# Revit family: 306_R4_D_
name_source: partatom
category: Pipe Accessories
units: mm (PartAtom-declared; Revit-internal decimal feet)

## family parameters
Always vertical = Yes
Cut with Voids When Loaded = No
Part Type = Valve - Breaks Into
Round Connector Dimension = Use Diameter
Shared = No
Work Plane-Based = No

## types (12) — shared parameters
CAT0 = Yes
Description = Characterised control valve, 2-way, External thread
L2D_Min = 3048 mm  [stored 10 ft]
Manufacturer = Belimo
QmdConnectorList = 301;D;302;D
magiPartTypeId = 306
magiProductFamilyId = R4*D*
zero-valued in all types: MC_Default_elevation

## per-type parameters (varying)
| type | BB | D | G1 | G2 | G3 | H | H1 | H1__ve | H2 | L1 | L2 | L2D | LL | W2D |
| R404DK | 14 mm  [stored 0.0459318 ft] | 10 mm | 23 mm | 14 mm  [stored 0.0459318 ft] | 11 mm | 38 mm  [stored 0.124672 ft] | 22 mm  [stored 0.0721785 ft] | -22 mm  [stored -0.0721785 ft] | 16 mm | 34 mm | 9 mm | 43 mm | 22 mm  [stored 0.0721785 ft] | 10 mm  [stored 0.0328084 ft] |
| R419D | 24 mm  [stored 0.0787402 ft] | 20 mm | 38 mm  [stored 0.124672 ft] | 24 mm  [stored 0.0787402 ft] | 19 mm  [stored 0.062336 ft] | 55 mm  [stored 0.180446 ft] | 31 mm | -31 mm | 24 mm  [stored 0.0787402 ft] | 57 mm | 14 mm  [stored 0.0459318 ft] | 71 mm | 36 mm | 20 mm  [stored 0.0656168 ft] |
| R418D | 24 mm  [stored 0.0787402 ft] | 20 mm | 38 mm  [stored 0.124672 ft] | 24 mm  [stored 0.0787402 ft] | 19 mm  [stored 0.062336 ft] | 55 mm  [stored 0.180446 ft] | 31 mm | -31 mm | 24 mm  [stored 0.0787402 ft] | 57 mm | 14 mm  [stored 0.0459318 ft] | 71 mm | 36 mm | 20 mm  [stored 0.0656168 ft] |
| R417D | 24 mm  [stored 0.0787402 ft] | 20 mm | 38 mm  [stored 0.124672 ft] | 24 mm  [stored 0.0787402 ft] | 19 mm  [stored 0.062336 ft] | 55 mm  [stored 0.180446 ft] | 31 mm | -31 mm | 24 mm  [stored 0.0787402 ft] | 57 mm | 14 mm  [stored 0.0459318 ft] | 71 mm | 36 mm | 20 mm  [stored 0.0656168 ft] |
| R414D | 19 mm  [stored 0.062336 ft] | 15 mm | 30 mm  [stored 0.0984252 ft] | 19 mm  [stored 0.062336 ft] | 15 mm  [stored 0.0492126 ft] | 42 mm  [stored 0.137795 ft] | 22 mm  [stored 0.0721785 ft] | -22 mm  [stored -0.0721785 ft] | 20 mm  [stored 0.0656168 ft] | 40 mm  [stored 0.131234 ft] | 10 mm  [stored 0.0328084 ft] | 50 mm | 25 mm  [stored 0.082021 ft] | 15 mm  [stored 0.0492126 ft] |
| R413D | 19 mm  [stored 0.062336 ft] | 15 mm | 30 mm  [stored 0.0984252 ft] | 19 mm  [stored 0.062336 ft] | 15 mm  [stored 0.0492126 ft] | 42 mm  [stored 0.137795 ft] | 22 mm  [stored 0.0721785 ft] | -22 mm  [stored -0.0721785 ft] | 20 mm  [stored 0.0656168 ft] | 40 mm  [stored 0.131234 ft] | 10 mm  [stored 0.0328084 ft] | 50 mm | 25 mm  [stored 0.082021 ft] | 15 mm  [stored 0.0492126 ft] |
| R412D | 19 mm  [stored 0.062336 ft] | 15 mm | 30 mm  [stored 0.0984252 ft] | 19 mm  [stored 0.062336 ft] | 15 mm  [stored 0.0492126 ft] | 42 mm  [stored 0.137795 ft] | 22 mm  [stored 0.0721785 ft] | -22 mm  [stored -0.0721785 ft] | 20 mm  [stored 0.0656168 ft] | 40 mm  [stored 0.131234 ft] | 10 mm  [stored 0.0328084 ft] | 50 mm | 25 mm  [stored 0.082021 ft] | 15 mm  [stored 0.0492126 ft] |
| R409DK | 14 mm  [stored 0.0459318 ft] | 10 mm | 23 mm | 14 mm  [stored 0.0459318 ft] | 11 mm | 38 mm  [stored 0.124672 ft] | 22 mm  [stored 0.0721785 ft] | -22 mm  [stored -0.0721785 ft] | 16 mm | 35 mm | 9 mm | 43 mm | 22 mm  [stored 0.0721785 ft] | 10 mm  [stored 0.0328084 ft] |
| R408DK | 14 mm  [stored 0.0459318 ft] | 10 mm | 23 mm | 14 mm  [stored 0.0459318 ft] | 11 mm | 38 mm  [stored 0.124672 ft] | 22 mm  [stored 0.0721785 ft] | -22 mm  [stored -0.0721785 ft] | 16 mm | 34 mm | 9 mm | 43 mm | 22 mm  [stored 0.0721785 ft] | 10 mm  [stored 0.0328084 ft] |
| R407DK | 14 mm  [stored 0.0459318 ft] | 10 mm | 23 mm | 14 mm  [stored 0.0459318 ft] | 11 mm | 38 mm  [stored 0.124672 ft] | 22 mm  [stored 0.0721785 ft] | -22 mm  [stored -0.0721785 ft] | 16 mm | 34 mm | 9 mm | 43 mm | 22 mm  [stored 0.0721785 ft] | 10 mm  [stored 0.0328084 ft] |
| R406DK | 14 mm  [stored 0.0459318 ft] | 10 mm | 23 mm | 14 mm  [stored 0.0459318 ft] | 11 mm | 38 mm  [stored 0.124672 ft] | 22 mm  [stored 0.0721785 ft] | -22 mm  [stored -0.0721785 ft] | 16 mm | 34 mm | 9 mm | 43 mm | 22 mm  [stored 0.0721785 ft] | 10 mm  [stored 0.0328084 ft] |
| R405DK | 14 mm  [stored 0.0459318 ft] | 10 mm | 23 mm | 14 mm  [stored 0.0459318 ft] | 11 mm | 38 mm  [stored 0.124672 ft] | 22 mm  [stored 0.0721785 ft] | -22 mm  [stored -0.0721785 ft] | 16 mm | 34 mm | 9 mm | 43 mm | 22 mm  [stored 0.0721785 ft] | 10 mm  [stored 0.0328084 ft] |

note: column(s) folded — value = type name in every type: magiProductCode, magiProductId

note: [stored X ft] marks values corroborated as IEEE doubles in the binary element streams (Revit-internal decimal feet)

## geometry (parser evidence)
native form markers: Sweep x2
no freeform markers — native parametric forms only
